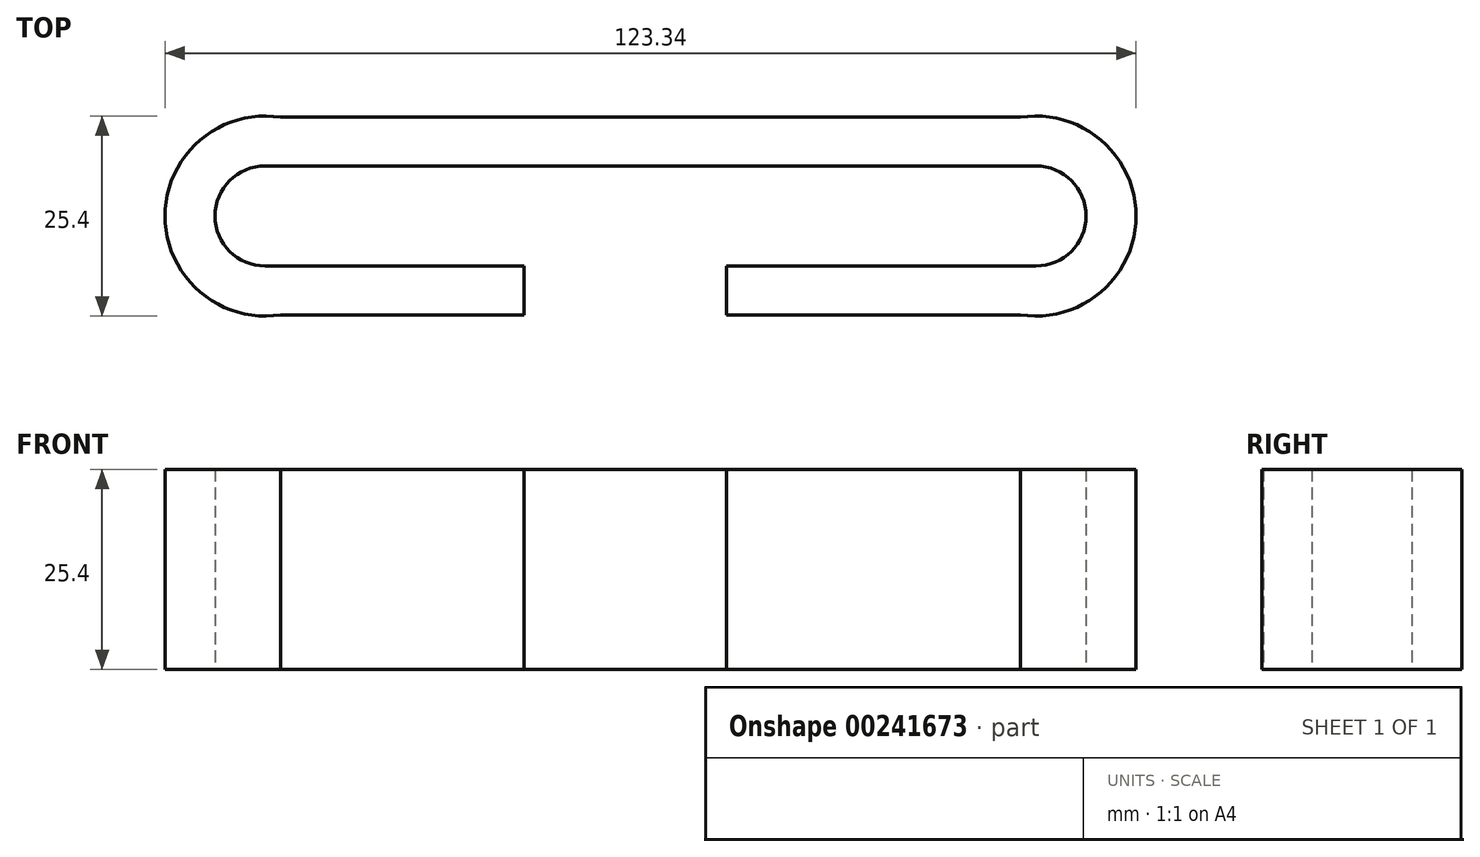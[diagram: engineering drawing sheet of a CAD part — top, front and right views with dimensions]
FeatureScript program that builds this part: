
annotation { "Feature Type Name" : "Feature", "Feature Type Description" : "" }
export const myFeature = defineFeature(function(context is Context, id is Id, definition is map)
    precondition{}
    {
        {
            var Q0;
            Q0=qCreatedBy(makeId("Top.planeOp"),FACE);
            var sketch = newSketch(context, id + "F0", { "sketchPlane" : qUnion([Q0])});
            skLineSegment(sketch, "E0.bottom", {"start": v(46.99, 12.54) * mm, "end": v(-46.99, 12.54) * mm});
            skLineSegment(sketch, "E0.top", {"start": v(46.99, -12.54) * mm, "end": v(9.64, -12.54) * mm});
            skPoint(sketch, "E0.middle", {"position": v(0, 0) * mm});
            skArc(sketch, "E1", {"start": v(-46.99, 12.54) * mm, "mid": v(-61.67, 0) * mm, "end": v(-46.99, -12.54) * mm});
            skArc(sketch, "E2", {"start": v(-48.97, 6.35) * mm, "mid": v(-55.32, 0) * mm, "end": v(-48.97, -6.35) * mm});
            skLineSegment(sketch, "E3", {"start": v(-48.97, 6.35) * mm, "end": v(48.97, 6.35) * mm});
            skLineSegment(sketch, "E4", {"start": v(-48.97, -6.35) * mm, "end": v(-16.04, -6.35) * mm});
            skArc(sketch, "E5", {"start": v(46.99, -12.54) * mm, "mid": v(61.67, 0) * mm, "end": v(46.99, 12.54) * mm});
            skLineSegment(sketch, "E6", {"start": v(-16.04, -6.35) * mm, "end": v(-16.04, -12.54) * mm});
            skLineSegment(sketch, "E7", {"start": v(9.64, -6.35) * mm, "end": v(9.64, -12.54) * mm});
            skLineSegment(sketch, "E8.trimOffspring", {"start": v(9.64, -6.35) * mm, "end": v(48.97, -6.35) * mm});
            skLineSegment(sketch, "E9.trimOffspring", {"start": v(-16.04, -12.54) * mm, "end": v(-46.99, -12.54) * mm});
            skPoint(sketch, "E10.orphan", {"position": v(48.97, -12.54) * mm});
            skPoint(sketch, "E11.orphan", {"position": v(48.97, 12.54) * mm});
            skArc(sketch, "E12", {"start": v(48.97, -6.35) * mm, "mid": v(55.32, 0) * mm, "end": v(48.97, 6.35) * mm});
            skPoint(sketch, "E13.orphan", {"position": v(-48.97, 12.54) * mm});
            skPoint(sketch, "E14.orphan", {"position": v(-48.97, -12.54) * mm});
            skSolve(sketch);
        }
        {
            var Q0;
            Q0 = qSketchRegion(id + "F0", true);
            extrude(context, id + "F1", {"entities" : qUnion([Q0]), "depth" : 25.4 * mm});
        }
    });
